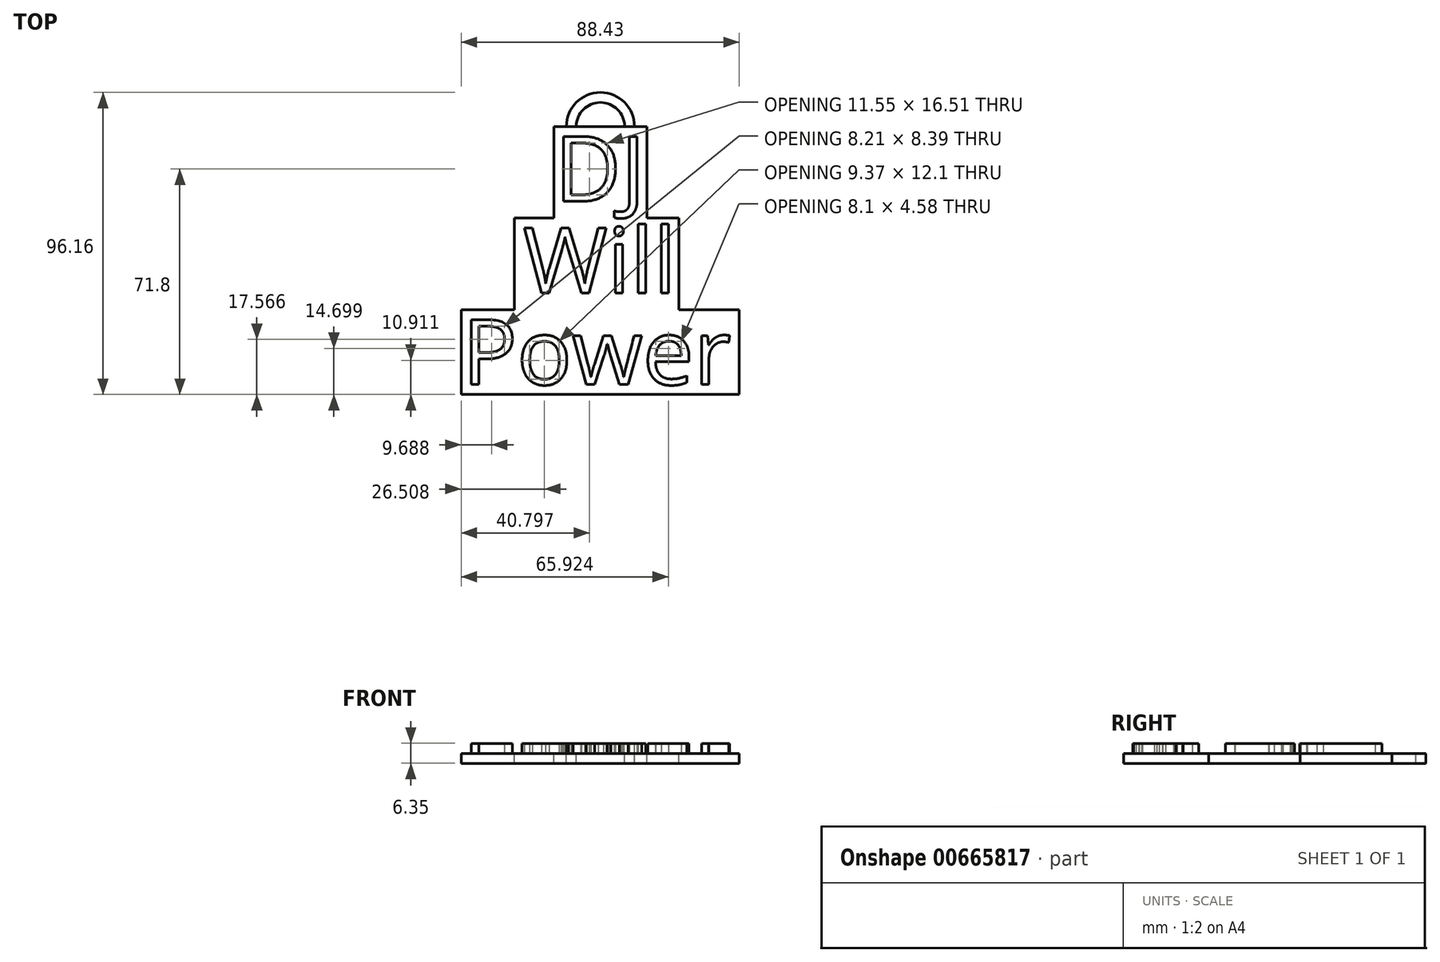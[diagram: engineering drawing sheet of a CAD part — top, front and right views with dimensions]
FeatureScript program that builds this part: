
annotation { "Feature Type Name" : "Feature", "Feature Type Description" : "" }
export const myFeature = defineFeature(function(context is Context, id is Id, definition is map)
    precondition{}
    {
        {
            var Q0;
            Q0=qCreatedBy(makeId("Top.planeOp"),FACE);
            var sketch = newSketch(context, id + "F0", { "sketchPlane" : qUnion([Q0])});
            skText(sketch, "E0", { "text": "DJ\n", "fontName": "OpenSans-Regular.ttf"});
            skText(sketch, "E1", { "text": "Will\n", "fontName": "OpenSans-Regular.ttf"});
            skText(sketch, "E2", { "text": "Power\n", "fontName": "OpenSans-Regular.ttf"});
            const initialGuessF0  = {"E0": [-0.01639, 0.02437, 1, 0, 0.02084], "E1": [-0.02643, -0.00477, 1, 0, 0.02084], "E2": [-0.04583, -0.03392, 1, 0, 0.02084]};
            skSetInitialGuess(sketch, initialGuessF0);
            skSolve(sketch);
        }
        {
            var Q0;
            Q0 = qSketchRegion(id + "F0", true);
            extrude(context, id + "F1", {"entities" : qUnion([Q0]), "depth" : 3.17 * mm, "offsetDistance" : 25.4 * mm});
        }
        {
            var Q0;
            Q0=makeQuery(id+"F1.opExtrude","CAP_FACE",FACE,{"disambiguationData":[OSD([sQuery(id+"F0.wireOp",EDGE,"E1.sketch_text.stroke-36"),sQuery(id+"F0.wireOp",EDGE,"E1.sketch_text.stroke-37"),sQuery(id+"F0.wireOp",EDGE,"E1.sketch_text.stroke-38"),sQuery(id+"F0.wireOp",EDGE,"E1.sketch_text.stroke-39")])],"isStart":true});
            var sketch = newSketch(context, id + "F2", { "sketchPlane" : qUnion([Q0])});
            skLineSegment(sketch, "E3.bottom", {"start": v(-46.17, 37.1) * mm, "end": v(42.26, 37.1) * mm});
            skLineSegment(sketch, "E3.top", {"start": v(-46.17, 10.08) * mm, "end": v(42.26, 10.08) * mm});
            skLineSegment(sketch, "E3.left", {"start": v(-46.17, 37.1) * mm, "end": v(-46.17, 10.08) * mm});
            skLineSegment(sketch, "E3.right", {"start": v(42.26, 37.1) * mm, "end": v(42.26, 10.08) * mm});
            skLineSegment(sketch, "E4.bottom", {"start": v(-29.23, 10.08) * mm, "end": v(23.02, 10.08) * mm});
            skLineSegment(sketch, "E4.top", {"start": v(-29.23, -19.07) * mm, "end": v(23.02, -19.07) * mm});
            skLineSegment(sketch, "E4.left", {"start": v(-29.23, 10.08) * mm, "end": v(-29.23, -19.07) * mm});
            skLineSegment(sketch, "E4.right", {"start": v(23.02, 10.08) * mm, "end": v(23.02, -19.07) * mm});
            skLineSegment(sketch, "E5.bottom", {"start": v(-16.72, -19.07) * mm, "end": v(12.98, -19.07) * mm});
            skLineSegment(sketch, "E5.top", {"start": v(-16.72, -48.22) * mm, "end": v(12.98, -48.22) * mm});
            skLineSegment(sketch, "E5.left", {"start": v(-16.72, -19.07) * mm, "end": v(-16.72, -48.22) * mm});
            skLineSegment(sketch, "E5.right", {"start": v(12.98, -19.07) * mm, "end": v(12.98, -48.22) * mm});
            skSolve(sketch);
        }
        {
            var Q0;
            Q0 = qSketchRegion(id + "F2", true);
            extrude(context, id + "F3", {"entities" : qUnion([Q0]), "depth" : 3.17 * mm, "offsetDistance" : 25.4 * mm});
        }
        {
            var Q0;
            Q0=makeQuery(id+"F3.opExtrude","CAP_FACE",FACE,{"disambiguationData":[OSD([sQuery(id+"F2.wireOp",EDGE,"E3.bottom"),sQuery(id+"F2.wireOp",EDGE,"E3.top"),sQuery(id+"F2.wireOp",EDGE,"E3.left"),sQuery(id+"F2.wireOp",EDGE,"E3.right"),sQuery(id+"F2.wireOp",EDGE,"E4.top"),sQuery(id+"F2.wireOp",EDGE,"E4.left"),sQuery(id+"F2.wireOp",EDGE,"E4.right"),sQuery(id+"F2.wireOp",EDGE,"E5.top"),sQuery(id+"F2.wireOp",EDGE,"E5.left"),sQuery(id+"F2.wireOp",EDGE,"E5.right")])],"isStart":true});
            var sketch = newSketch(context, id + "F4", { "sketchPlane" : qUnion([Q0])});
            skPoint(sketch, "E6.centerSnap0", {"position": v(-1.87, 48.22) * mm});
            skArc(sketch, "E7", {"start": v(-1.87, 59.06) * mm, "mid": v(-9.54, 55.88) * mm, "end": v(-12.71, 48.22) * mm});
            skArc(sketch, "E8", {"start": v(-1.87, 59.06) * mm, "mid": v(5.8, 55.88) * mm, "end": v(8.97, 48.22) * mm});
            skArc(sketch, "E9", {"start": v(-1.87, 55.88) * mm, "mid": v(-7.3, 53.64) * mm, "end": v(-9.54, 48.22) * mm});
            skPoint(sketch, "E9.startSnap0", {"position": v(-9.54, 55.88) * mm});
            skArc(sketch, "E10", {"start": v(-1.87, 55.88) * mm, "mid": v(3.55, 53.64) * mm, "end": v(5.8, 48.22) * mm});
            skSolve(sketch);
        }
        {
            var Q0;
            {var subQ3=sQuery(id+"F4.wireOp",EDGE,"E7");Q0=makeQuery(id+"F4.imprint","IMPRINT",FACE,{"disambiguationData":[TD([[makeQuery(id+"F4.imprint","IMPRINT",EDGE,{"derivedFrom":subQ3}),1.0]])]});}
            extrude(context, id + "F5", {"entities" : qUnion([Q0]), "oppositeDirection" : true, "depth" : 3.17 * mm, "offsetDistance" : 25.4 * mm});
        }
    });
